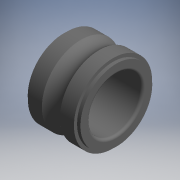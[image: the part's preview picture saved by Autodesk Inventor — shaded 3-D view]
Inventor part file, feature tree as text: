
AUTODESK INVENTOR PART (.ipt)
format: ipt  version: 2017.3 (Build 213256000, 256)  size: 164,864 bytes
history: native  units: mm (DEFAULTED — no unit token found)
features: other x70, revolve x1, sketch x1
ambient origin geometry x8: Origin, YZ Plane, XZ Plane, XY Plane, X Axis, Y Axis, Z Axis, Center Point
bodies: Solid1 (feature_tree)
feature tree (72):
  revolve  "Revolution1"  [1 undecoded]
  other  "ip_st_1_1_XY"
  other  "ip_st_1_1_YZ"
  other  "ip_st_1_1_ZX"
  other  "ip_st_1_1_X"
  other  "ip_st_1_1_Y"
  other  "ip_st_1_1_Z"
  other  "ip_st_1_1_Center"
  other  "ip_st_1_2_XY"
  other  "ip_st_1_2_YZ"
  other  "ip_st_1_2_ZX"
  other  "ip_st_1_2_X"
  other  "ip_st_1_2_Y"
  other  "ip_st_1_2_Z"
  other  "ip_st_1_2_Center"
  other  "ip_st_1_3_XY"
  other  "ip_st_1_3_YZ"
  other  "ip_st_1_3_ZX"
  other  "ip_st_1_3_X"
  other  "ip_st_1_3_Y"
  other  "ip_st_1_3_Z"
  other  "ip_st_1_3_Center"
  other  "ip_st_1_4_XY"
  other  "ip_st_1_4_YZ"
  other  "ip_st_1_4_ZX"
  other  "ip_st_1_4_X"
  other  "ip_st_1_4_Y"
  other  "ip_st_1_4_Z"
  other  "ip_st_1_4_Center"
  other  "ip_st_1_5_XY"
  other  "ip_st_1_5_YZ"
  other  "ip_st_1_5_ZX"
  other  "ip_st_1_5_X"
  other  "ip_st_1_5_Y"
  other  "ip_st_1_5_Z"
  other  "ip_st_1_5_Center"
  other  "ip_st_1_6_XY"
  other  "ip_st_1_6_YZ"
  other  "ip_st_1_6_ZX"
  other  "ip_st_1_6_X"
  other  "ip_st_1_6_Y"
  other  "ip_st_1_6_Z"
  other  "ip_st_1_6_Center"
  other  "ip_st_1_7_XY"
  other  "ip_st_1_7_YZ"
  other  "ip_st_1_7_ZX"
  other  "ip_st_1_7_X"
  other  "ip_st_1_7_Y"
  other  "ip_st_1_7_Z"
  other  "ip_st_1_7_Center"
  other  "ip_st_1_8_XY"
  other  "ip_st_1_8_YZ"
  other  "ip_st_1_8_ZX"
  other  "ip_st_1_8_X"
  other  "ip_st_1_8_Y"
  other  "ip_st_1_8_Z"
  other  "ip_st_1_8_Center"
  other  "ip_st_1a_XY"
  other  "ip_st_1a_YZ"
  other  "ip_st_1a_ZX"
  other  "ip_st_1a_X"
  other  "ip_st_1a_Y"
  other  "ip_st_1a_Z"
  other  "ip_st_1a_Center"
  other  "ip_st_2a_XY"
  other  "ip_st_2a_YZ"
  other  "ip_st_2a_ZX"
  other  "ip_st_2a_X"
  other  "ip_st_2a_Y"
  other  "ip_st_2a_Z"
  other  "ip_st_2a_Center"
  sketch  "Sketch_2"  dims[d0=360.0deg d1=0.0mm d2=0.0mm]
note: 1 required parameter value undecoded (feature->parameter linkage not recoverable at this tier; creation-order binding heuristic only, values carry confidence <= 0.55)
